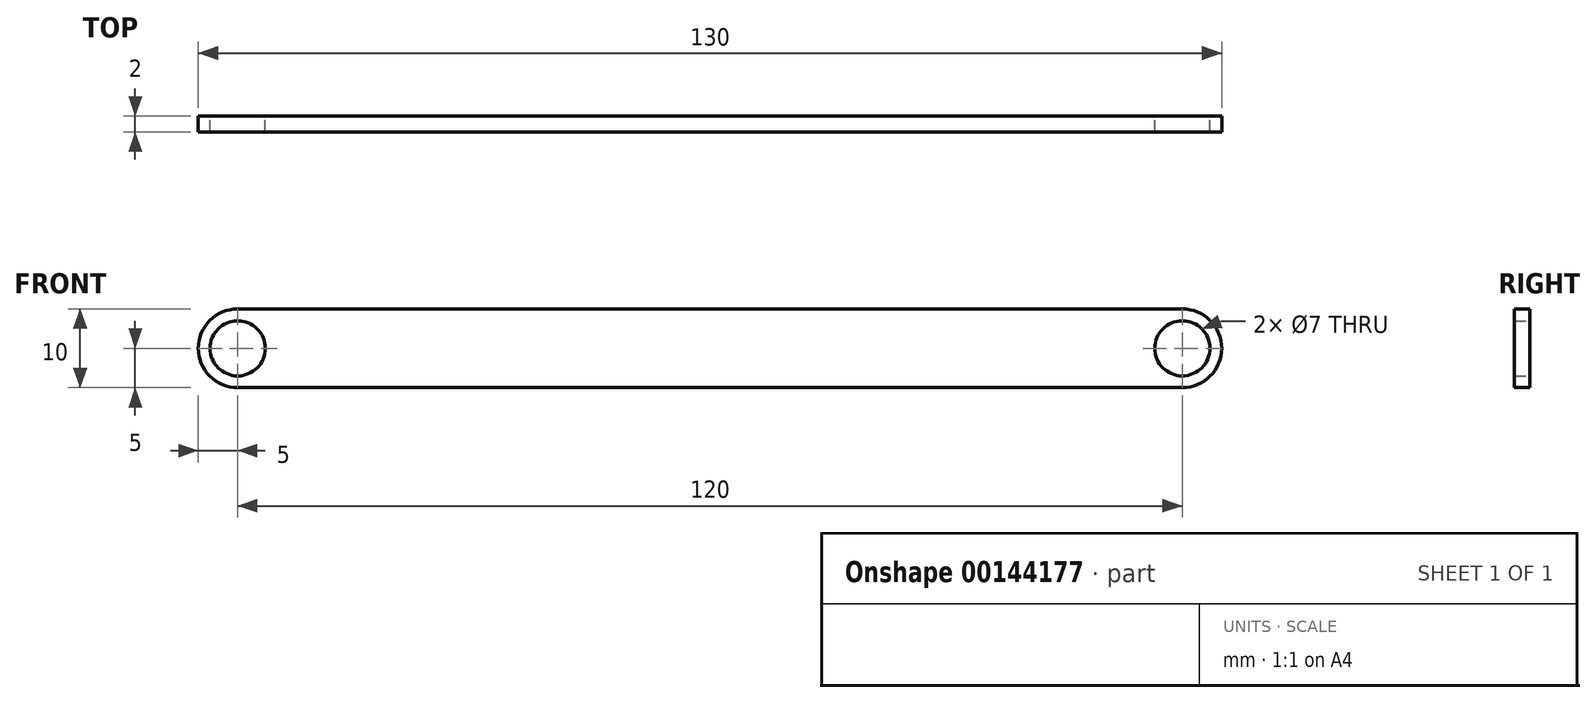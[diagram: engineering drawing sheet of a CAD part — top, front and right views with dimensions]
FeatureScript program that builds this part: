
annotation { "Feature Type Name" : "Feature", "Feature Type Description" : "" }
export const myFeature = defineFeature(function(context is Context, id is Id, definition is map)
    precondition{}
    {
        {
            var Q0;
            Q0=qCreatedBy(makeId("Front.planeOp"),FACE);
            var sketch = newSketch(context, id + "F0", { "sketchPlane" : qUnion([Q0])});
            skLineSegment(sketch, "E0", {"start": v(0, 0) * mm, "end": v(120, 0) * mm});
            skLineSegment(sketch, "E1", {"start": v(0, -10) * mm, "end": v(120, -10) * mm});
            skArc(sketch, "E2", {"start": v(0, 0) * mm, "mid": v(-5, -5) * mm, "end": v(0, -10) * mm});
            skArc(sketch, "E3", {"start": v(120, -10) * mm, "mid": v(125, -5) * mm, "end": v(120, 0) * mm});
            skCircle(sketch, "E4", {"center": v(0, -5) * mm, "radius": 3.5 * mm});
            skCircle(sketch, "E5", {"center": v(120, -5) * mm, "radius": 3.5 * mm});
            skSolve(sketch);
        }
        {
            var Q0;
            Q0=makeQuery(id+"F0.imprint","IMPRINT",FACE,{"disambiguationData":[TD([[makeQuery(id+"F0.imprint","IMPRINT",EDGE,{"derivedFrom":sQuery(id+"F0.wireOp",EDGE,"E0")}),-1.0]])]});
            extrude(context, id + "F1", {"entities" : qUnion([Q0]), "depth" : 2 * mm});
        }
    });
